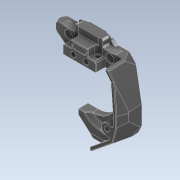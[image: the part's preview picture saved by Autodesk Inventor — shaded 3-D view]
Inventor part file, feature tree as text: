
AUTODESK INVENTOR PART (.ipt)
format: ipt  version: 2022.1 (Build 261234020, 234B)  size: 1,085,440 bytes
history: native  units: mm
features: sketch x3, extrude x2, delete_face x2, chamfer x2, direct_edit x1, hole x1, imported_body x1, move_body x1
ambient origin geometry x8: Origin, YZ Plane, XZ Plane, XY Plane, X Axis, Y Axis, Z Axis, Center Point
bodies: Volumenkörper1 (feature_tree)
feature tree (13):
  direct_edit  "Direktbearbeitung1"
  extrude  "Extrusion1"  Depth=10.0mm
  delete_face  "Fläche löschen1"
  chamfer  "Fase1"  Distance=10.0mm
  delete_face  "Fläche löschen2"
  extrude  "Extrusion2"  Depth=10.0mm TaperAngle=0.0deg
  hole  "Bohrung1"  [1 undecoded]
  chamfer  "Fase3"  [1 undecoded]
  sketch  "Skizze1"  dims[d0=0.0mm d1=0.0mm d2=0.2mm d3=3.1mm d4=10.0mm d5=0.0mm]
  sketch  "Skizze2"  dims[d6=0.4mm d7=2.0mm d8=45.0deg d9=10.0mm d10=0.0mm]
  sketch  "Skizze3"  dims[d11=3.399999mm d12=3.3mm d13=6.0mm d14=5.7mm d15=3.4mm d16=90.0deg d17=8.0mm d18=20.594885mm d22=0.4mm d23=2.0mm d24=45.0deg]
  imported_body  "Basis1"
  move_body  "Verschieben1"
note: 2 required parameter values undecoded (feature->parameter linkage not recoverable at this tier; creation-order binding heuristic only, values carry confidence <= 0.55)
